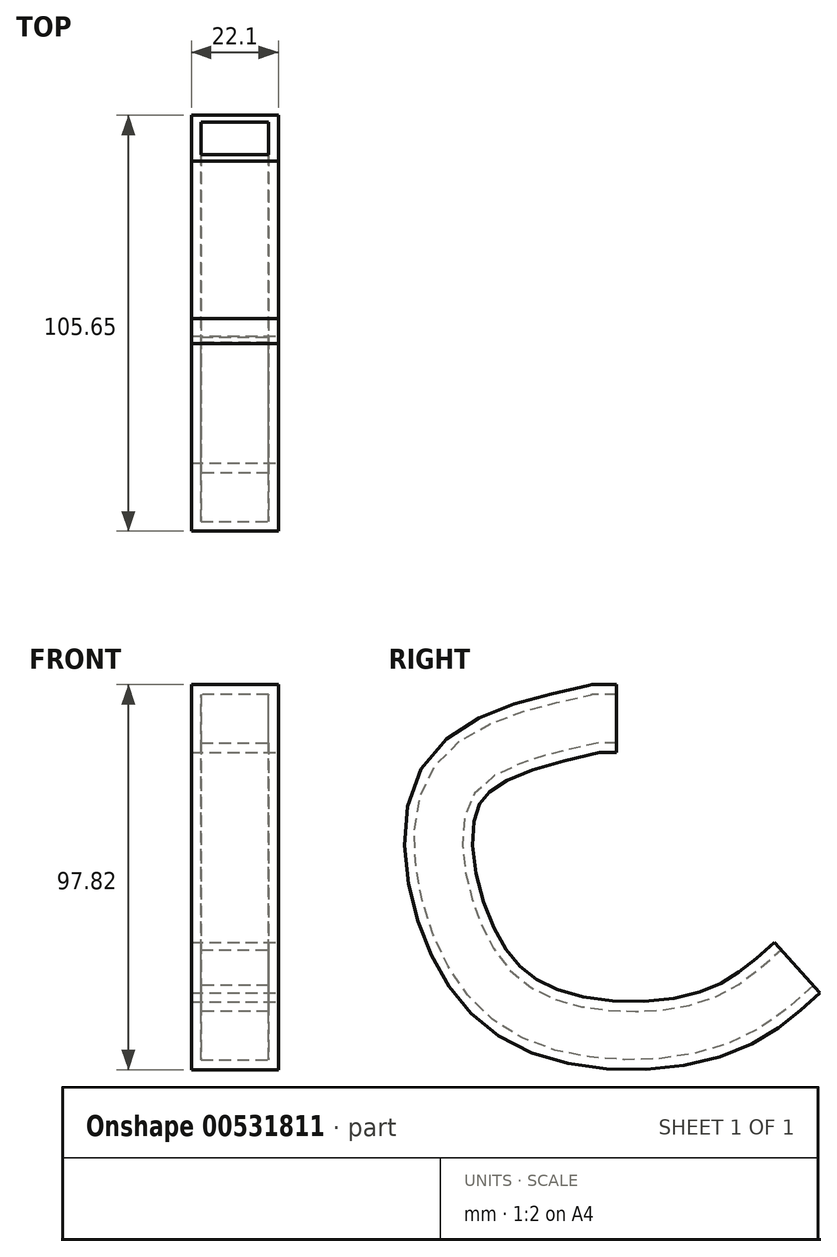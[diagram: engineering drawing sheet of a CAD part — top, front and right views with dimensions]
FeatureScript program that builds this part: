
annotation { "Feature Type Name" : "Feature", "Feature Type Description" : "" }
export const myFeature = defineFeature(function(context is Context, id is Id, definition is map)
    precondition{}
    {
        {
            var Q0;
            Q0=qCreatedBy(makeId("Front.planeOp"),FACE);
            var sketch = newSketch(context, id + "F0", { "sketchPlane" : qUnion([Q0])});
            skLineSegment(sketch, "E0.bottom", {"start": v(0, 27.76) * mm, "end": v(22.1, 27.76) * mm});
            skLineSegment(sketch, "E0.top", {"start": v(0, 45.04) * mm, "end": v(22.1, 45.04) * mm});
            skLineSegment(sketch, "E0.left", {"start": v(0, 27.76) * mm, "end": v(0, 45.04) * mm});
            skLineSegment(sketch, "E0.right", {"start": v(22.1, 27.76) * mm, "end": v(22.1, 45.04) * mm});
            skSolve(sketch);
        }
        {
            var Q0;
            Q0=qCreatedBy(makeId("Right.planeOp"),FACE);
            var sketch = newSketch(context, id + "F1", { "sketchPlane" : qUnion([Q0])});
            skLineSegment(sketch, "E1", {"start": v(0, 36.83) * mm, "end": v(-5.38, 36.83) * mm});
            skFitSpline(sketch, "E2", {"points": [v(-5.38, 36.83) * mm, v(-42.2, 20.11) * mm, v(-40.8, -17.56) * mm, v(-18.7, -40.8) * mm, v(24.08, -41.64) * mm, v(46.17, -27.2) * mm], "startDerivative": vector(-215.41, -47.05) * mm, "endDerivative": vector(108.13, 98.32) * mm});
            skSolve(sketch);
        }
        {
            var Q0;
            Q0 = qSketchRegion(id + "F0", true);
            var Q1;
            Q1 = qConstructionFilter(qBodyType(qCreatedBy(id + "F1" ,EDGE), BodyType.WIRE), ConstructionObject.NO);
            sweep(context, id + "F2", {"profiles" : qUnion([Q0]), "path" : qUnion([Q1])});
        }
        {
            var Q0;
            Q0=makeQuery(id+"F2.opSweep","CAP_FACE",FACE,{"disambiguationData":[OSD([sQuery(id+"F0.wireOp",EDGE,"E0.bottom"),sQuery(id+"F0.wireOp",EDGE,"E0.top"),sQuery(id+"F0.wireOp",EDGE,"E0.left"),sQuery(id+"F0.wireOp",EDGE,"E0.right"),sQuery(id+"F1.wireOp",VERTEX,"E1.start")])],"isStart":true});
            var Q1;
            Q1=makeQuery(id+"F2.opSweep","CAP_FACE",FACE,{"disambiguationData":[OSD([sQuery(id+"F0.wireOp",EDGE,"E0.bottom"),sQuery(id+"F0.wireOp",EDGE,"E0.top"),sQuery(id+"F0.wireOp",EDGE,"E0.left"),sQuery(id+"F0.wireOp",EDGE,"E0.right"),sQuery(id+"F1.wireOp",VERTEX,"E2.end")])],"isStart":false});
            shell(context, id + "F3", {"entities" : qUnion([Q0, Q1]), "thickness" : 2.5 * mm});
        }
    });
